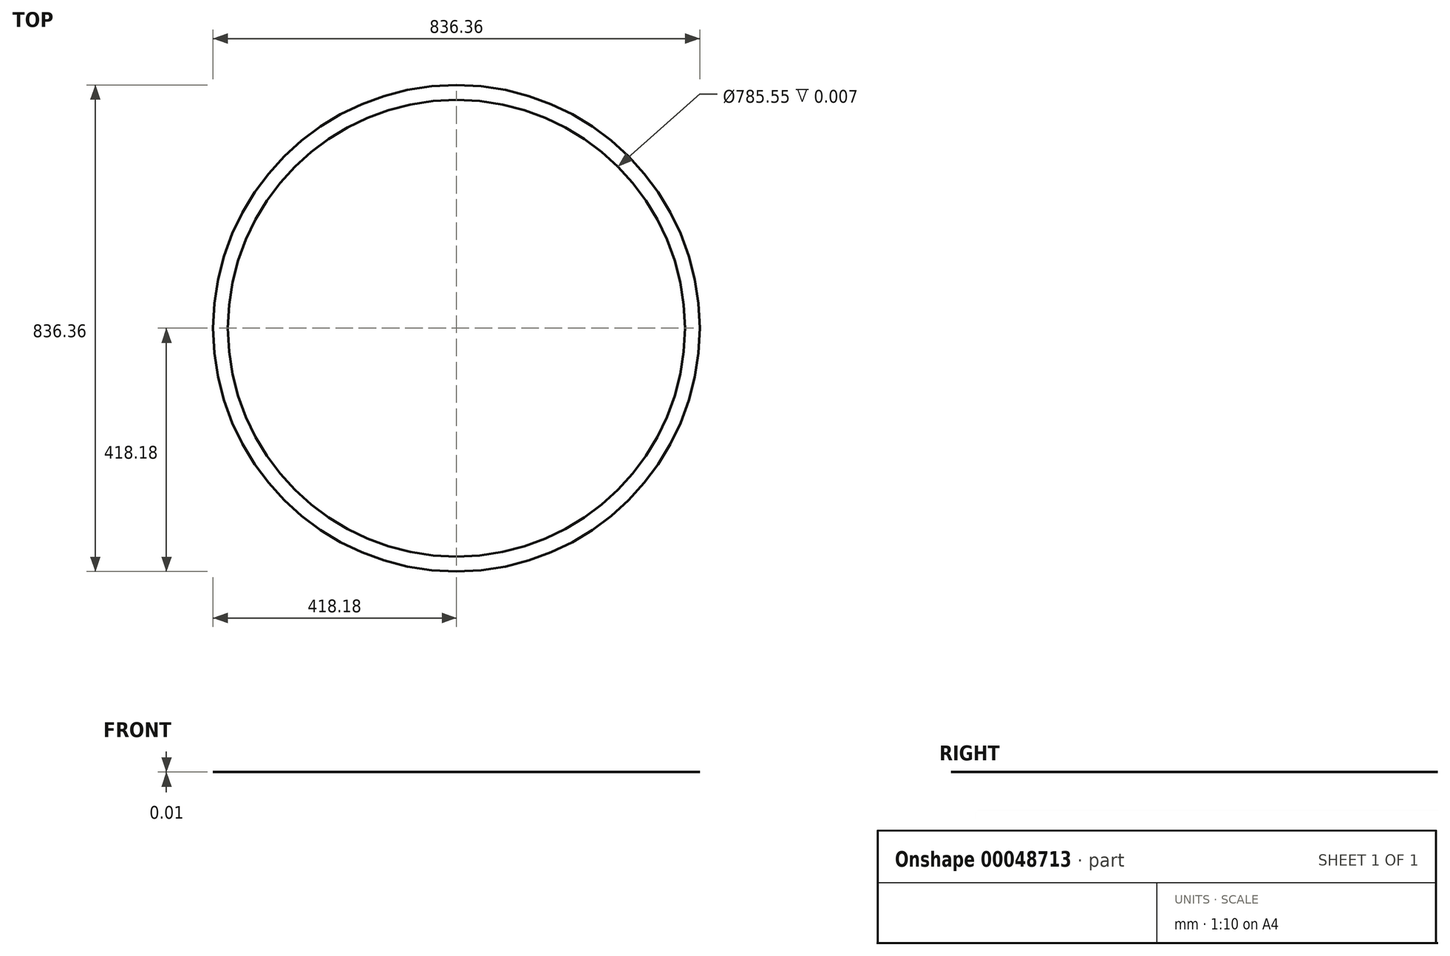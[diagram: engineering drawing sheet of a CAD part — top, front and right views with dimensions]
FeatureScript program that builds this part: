
annotation { "Feature Type Name" : "Feature", "Feature Type Description" : "" }
export const myFeature = defineFeature(function(context is Context, id is Id, definition is map)
    precondition{}
    {
        {
            var Q0;
            Q0=qCreatedBy(makeId("Top.planeOp"),FACE);
            var sketch = newSketch(context, id + "F0", { "sketchPlane" : qUnion([Q0])});
            skCircle(sketch, "E0", {"center": v(0, 0) * mm, "radius": 418.18 * mm});
            skCircle(sketch, "E1", {"center": v(0, 0) * mm, "radius": 392.78 * mm});
            skSolve(sketch);
        }
        {
            var Q0;
            Q0 = qSketchRegion(id + "F0", true);
            extrude(context, id + "F1", {"entities" : qUnion([Q0]), "depth" : 3 / 457.2 * mm});
        }
    });
